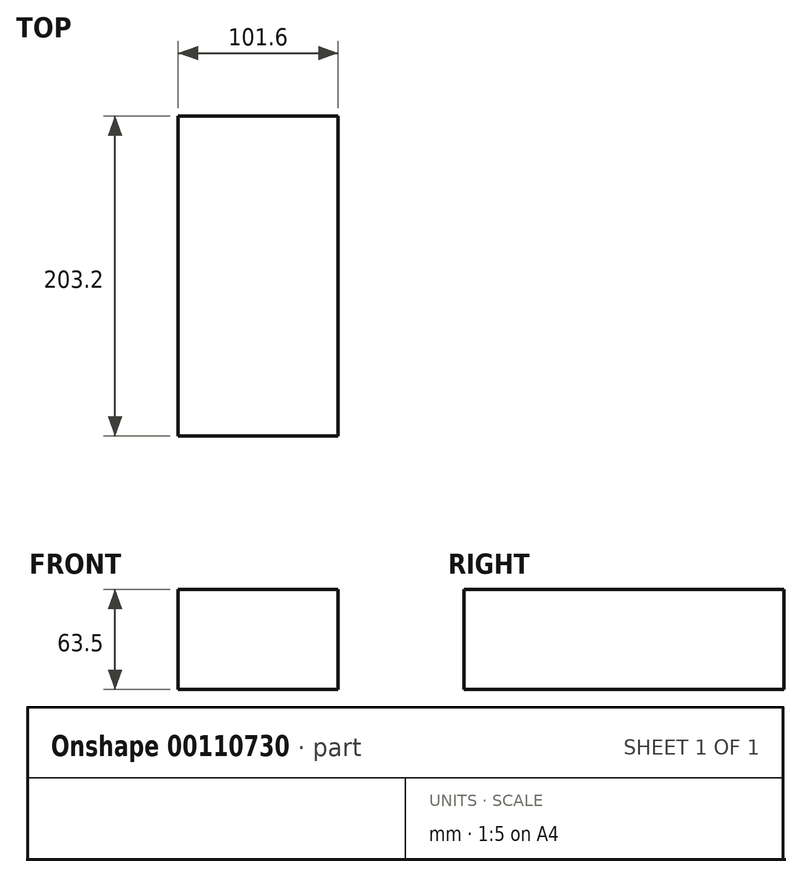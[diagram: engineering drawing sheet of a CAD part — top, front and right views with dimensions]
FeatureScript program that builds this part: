
annotation { "Feature Type Name" : "Feature", "Feature Type Description" : "" }
export const myFeature = defineFeature(function(context is Context, id is Id, definition is map)
    precondition{}
    {
        {
            var Q0;
            Q0=qCreatedBy(makeId("Front.planeOp"),FACE);
            var sketch = newSketch(context, id + "F0", { "sketchPlane" : qUnion([Q0])});
            skLineSegment(sketch, "E0", {"start": v(0, 0) * mm, "end": v(101.6, 0) * mm});
            skLineSegment(sketch, "E1", {"start": v(101.6, 0) * mm, "end": v(101.6, 63.5) * mm});
            skLineSegment(sketch, "E2", {"start": v(101.6, 63.5) * mm, "end": v(0, 63.5) * mm});
            skLineSegment(sketch, "E3", {"start": v(0, 63.5) * mm, "end": v(0, 0) * mm});
            skSolve(sketch);
        }
        {
            var Q0;
            Q0=makeQuery(id+"F0.imprint","IMPRINT",FACE,{"disambiguationData":[TD([[makeQuery(id+"F0.imprint","IMPRINT",EDGE,{"derivedFrom":sQuery(id+"F0.wireOp",EDGE,"E0")}),1.0]])]});
            extrude(context, id + "F1", {"entities" : qUnion([Q0]), "depth" : 203.2 * mm});
        }
    });
